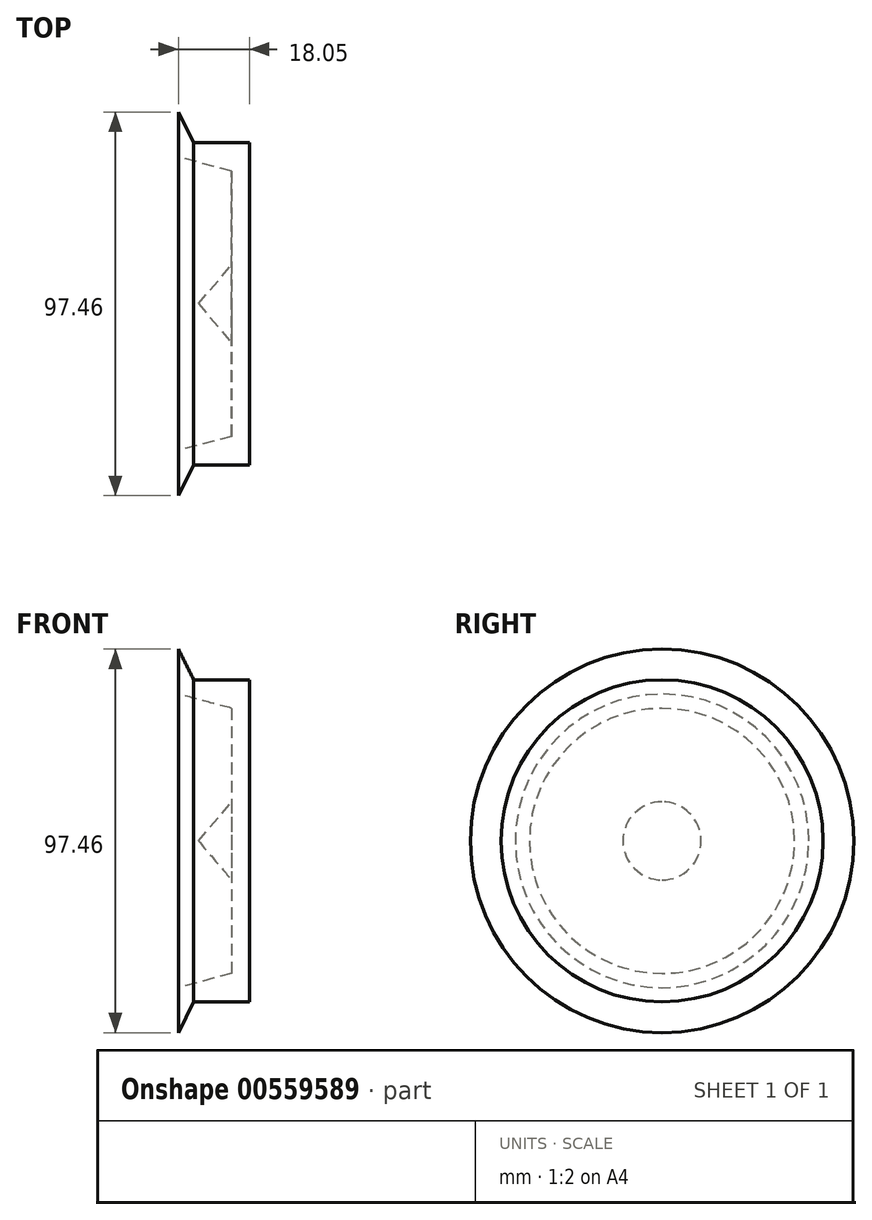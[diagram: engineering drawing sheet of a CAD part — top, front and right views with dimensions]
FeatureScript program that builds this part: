
annotation { "Feature Type Name" : "Feature", "Feature Type Description" : "" }
export const myFeature = defineFeature(function(context is Context, id is Id, definition is map)
    precondition{}
    {
        {
            var Q0;
            Q0=qCreatedBy(makeId("Top.planeOp"),FACE);
            var sketch = newSketch(context, id + "F0", { "sketchPlane" : qUnion([Q0])});
            skLineSegment(sketch, "E0", {"start": v(0, 40.9) * mm, "end": v(-14.14, 40.9) * mm});
            skLineSegment(sketch, "E1", {"start": v(-14.14, 40.9) * mm, "end": v(-18.05, 48.73) * mm});
            skLineSegment(sketch, "E2", {"start": v(-18.05, 48.73) * mm, "end": v(-18.05, 37.3) * mm});
            skLineSegment(sketch, "E3", {"start": v(-18.05, 37.3) * mm, "end": v(-4.51, 33.69) * mm});
            skLineSegment(sketch, "E4", {"start": v(-4.51, 33.69) * mm, "end": v(-4.51, 9.93) * mm});
            skLineSegment(sketch, "E5", {"start": v(-4.51, 9.93) * mm, "end": v(-12.93, 0) * mm});
            skLineSegment(sketch, "E6", {"start": v(-12.93, 0) * mm, "end": v(0, 0) * mm});
            skLineSegment(sketch, "E7", {"start": v(0, 40.9) * mm, "end": v(0, 0) * mm});
            skSolve(sketch);
        }
        {
            var Q0;
            Q0=makeQuery(id+"F0.imprint","IMPRINT",FACE,{"disambiguationData":[TD([[makeQuery(id+"F0.imprint","IMPRINT",EDGE,{"derivedFrom":sQuery(id+"F0.wireOp",EDGE,"E0")}),1.0]])]});
            var Q1;
            Q1=sQuery(id+"F0.wireOp",EDGE,"E6");
            revolve(context, id + "F1", {"entities" : qUnion([Q0]), "axis" : qUnion([Q1]), "revolveType" : RevolveType.FULL});
        }
    });
